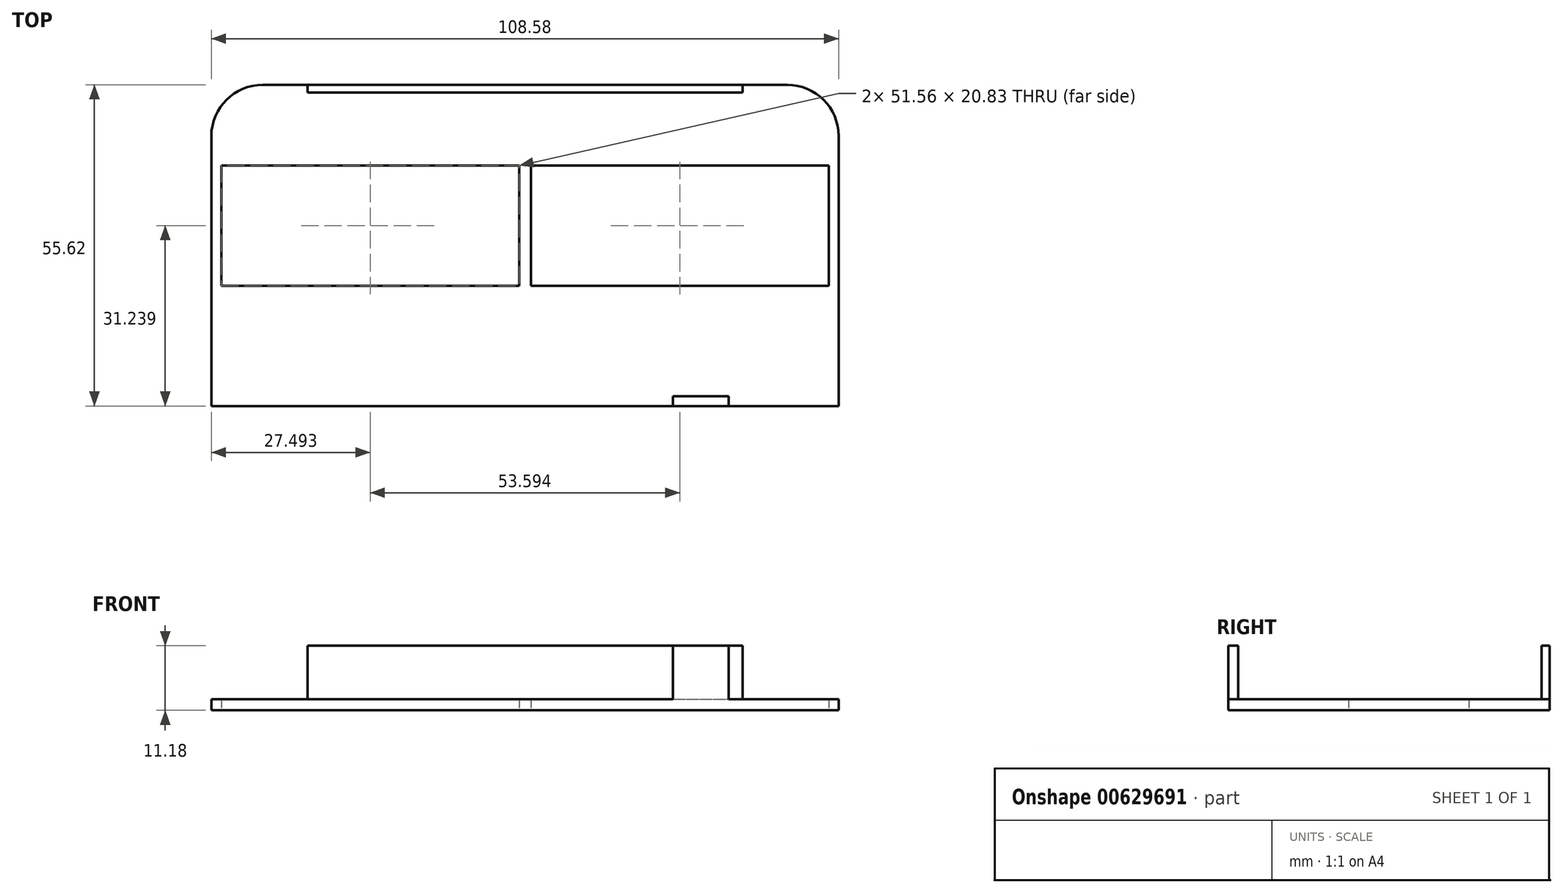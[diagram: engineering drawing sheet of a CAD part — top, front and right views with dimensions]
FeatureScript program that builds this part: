
annotation { "Feature Type Name" : "Feature", "Feature Type Description" : "" }
export const myFeature = defineFeature(function(context is Context, id is Id, definition is map)
    precondition{}
    {
        {
            var Q0;
            Q0=qCreatedBy(makeId("Top.planeOp"),FACE);
            var sketch = newSketch(context, id + "F0", { "sketchPlane" : qUnion([Q0])});
            skLineSegment(sketch, "E0.bottom", {"start": v(45.4, 27.81) * mm, "end": v(-45.4, 27.81) * mm});
            skLineSegment(sketch, "E0.top", {"start": v(54.3, -27.81) * mm, "end": v(-54.3, -27.81) * mm});
            skLineSegment(sketch, "E0.left", {"start": v(54.3, 18.92) * mm, "end": v(54.3, -27.81) * mm});
            skLineSegment(sketch, "E0.right", {"start": v(-54.3, 18.92) * mm, "end": v(-54.3, -27.81) * mm});
            skPoint(sketch, "E0.middle", {"position": v(0, 0) * mm});
            skPoint(sketch, "E1.visualSharp", {"position": v(-54.3, 27.81) * mm});
            skArc(sketch, "E1.filletArc", {"start": v(-45.4, 27.81) * mm, "mid": v(-51.69, 25.2) * mm, "end": v(-54.3, 18.92) * mm});
            skPoint(sketch, "E2.visualSharp", {"position": v(54.3, 27.81) * mm});
            skArc(sketch, "E2.filletArc", {"start": v(54.3, 18.92) * mm, "mid": v(51.69, 25.2) * mm, "end": v(45.4, 27.81) * mm});
            skLineSegment(sketch, "E3.bottom", {"start": v(-52.58, 13.84) * mm, "end": v(-1.02, 13.84) * mm});
            skLineSegment(sketch, "E3.top", {"start": v(-52.58, -6.98) * mm, "end": v(-1.02, -6.98) * mm});
            skLineSegment(sketch, "E3.left", {"start": v(-52.58, 13.84) * mm, "end": v(-52.58, -6.98) * mm});
            skLineSegment(sketch, "E3.right", {"start": v(-1.02, 13.84) * mm, "end": v(-1.02, -6.98) * mm});
            skLineSegment(sketch, "E4.bottom", {"start": v(1.02, 13.84) * mm, "end": v(52.58, 13.84) * mm});
            skLineSegment(sketch, "E4.left", {"start": v(1.02, 13.84) * mm, "end": v(1.02, -6.98) * mm});
            skLineSegment(sketch, "E4.right", {"start": v(52.58, 13.84) * mm, "end": v(52.58, -6.98) * mm});
            skLineSegment(sketch, "E5", {"start": v(0, 0) * mm, "end": v(0, 13.84) * mm, "construction": true});
            skLineSegment(sketch, "E6", {"start": v(-1.02, 13.84) * mm, "end": v(1.02, 13.84) * mm, "construction": true});
            skLineSegment(sketch, "E7", {"start": v(1.02, -6.98) * mm, "end": v(52.58, -6.98) * mm});
            skSolve(sketch);
        }
        {
            var Q0;
            Q0 = qSketchRegion(id + "F0", true);
            extrude(context, id + "F1", {"entities" : qUnion([Q0]), "depth" : 1.9 * mm, "offsetDistance" : 25.4 * mm});
        }
        {
            var Q0;
            Q0=makeQuery(id+"F1.opExtrude","CAP_FACE",FACE,{"disambiguationData":[OSD([sQuery(id+"F0.wireOp",EDGE,"E0.bottom"),sQuery(id+"F0.wireOp",EDGE,"E0.top"),sQuery(id+"F0.wireOp",EDGE,"E0.left"),sQuery(id+"F0.wireOp",EDGE,"E0.right"),sQuery(id+"F0.wireOp",EDGE,"E1.filletArc"),sQuery(id+"F0.wireOp",EDGE,"E2.filletArc"),sQuery(id+"F0.wireOp",EDGE,"E3.bottom"),sQuery(id+"F0.wireOp",EDGE,"E3.top"),sQuery(id+"F0.wireOp",EDGE,"E3.left"),sQuery(id+"F0.wireOp",EDGE,"E3.right"),sQuery(id+"F0.wireOp",EDGE,"E4.bottom"),sQuery(id+"F0.wireOp",EDGE,"E4.left"),sQuery(id+"F0.wireOp",EDGE,"E4.right"),sQuery(id+"F0.wireOp",EDGE,"E7")])],"isStart":false});
            var sketch = newSketch(context, id + "F2", { "sketchPlane" : qUnion([Q0])});
            skLineSegment(sketch, "E8.bottom", {"start": v(-37.66, 27.81) * mm, "end": v(37.66, 27.81) * mm});
            skLineSegment(sketch, "E8.top", {"start": v(-37.66, 26.44) * mm, "end": v(37.66, 26.44) * mm});
            skLineSegment(sketch, "E8.left", {"start": v(-37.66, 27.81) * mm, "end": v(-37.66, 26.44) * mm});
            skLineSegment(sketch, "E8.right", {"start": v(37.66, 27.81) * mm, "end": v(37.66, 26.44) * mm});
            skLineSegment(sketch, "E9", {"start": v(0, 0) * mm, "end": v(0, 26.44) * mm, "construction": true});
            skLineSegment(sketch, "E10.bottom", {"start": v(35.24, -27.81) * mm, "end": v(25.63, -27.81) * mm});
            skLineSegment(sketch, "E10.top", {"start": v(35.24, -26.1) * mm, "end": v(25.63, -26.1) * mm});
            skLineSegment(sketch, "E10.left", {"start": v(35.24, -27.81) * mm, "end": v(35.24, -26.1) * mm});
            skLineSegment(sketch, "E10.right", {"start": v(25.63, -27.81) * mm, "end": v(25.63, -26.1) * mm});
            skSolve(sketch);
        }
        {
            var Q0;
            Q0 = qSketchRegion(id + "F2", true);
            extrude(context, id + "F3", {"entities" : qUnion([Q0]), "operationType" : NewBodyOperationType.ADD, "depth" : 9.27 * mm, "offsetDistance" : 25.4 * mm});
        }
    });
